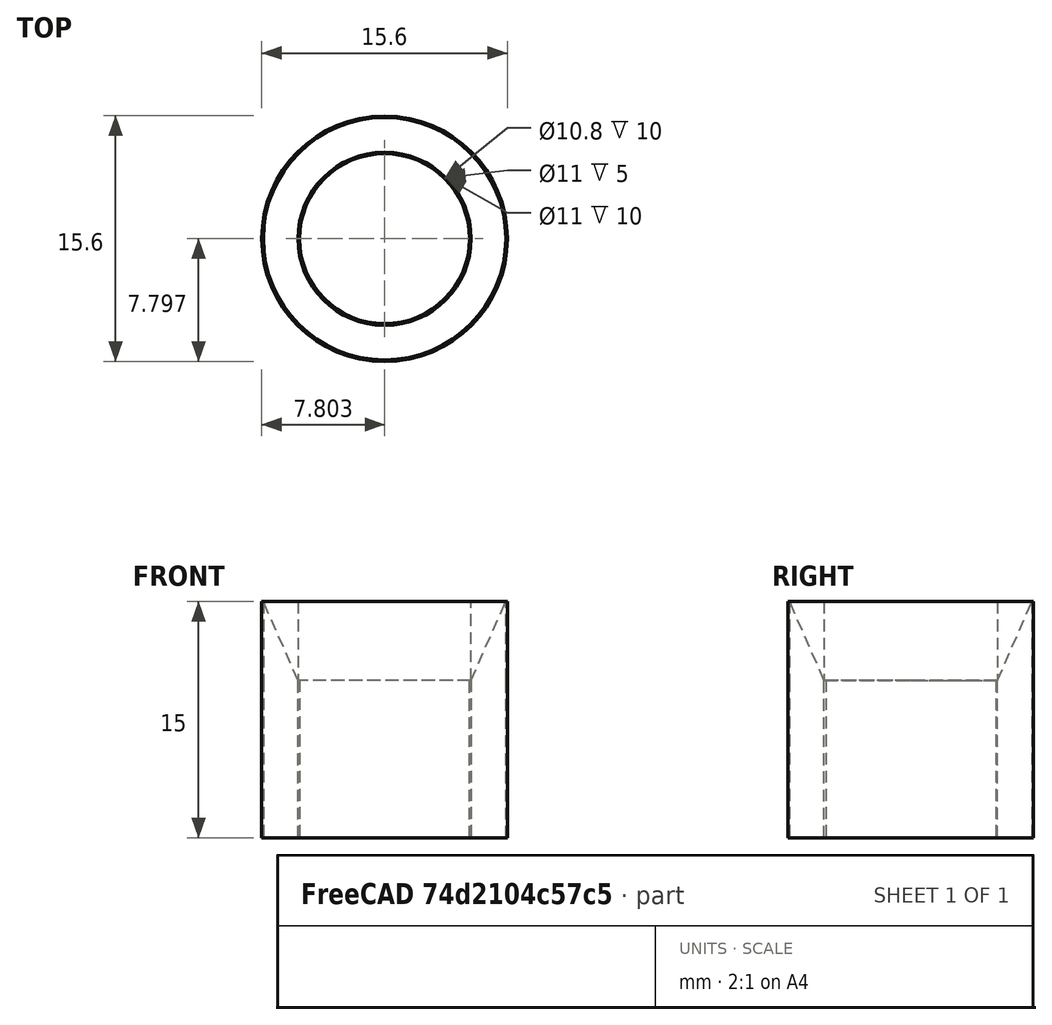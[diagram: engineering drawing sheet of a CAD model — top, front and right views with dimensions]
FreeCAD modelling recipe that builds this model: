
FCSTD DOCUMENT  (FreeCAD 0.18.4R)
Label: spillway.reducer
License: All rights reserved
LicenseURL: http://en.wikipedia.org/wiki/All_rights_reserved
objects: Part::Extrusion×6, Part::Part2DObjectPython×4, Part::Feature×4, Part::Cut×3, Part::MultiFuse×3
note: 20 computed .brp shape members not serialized (recipe doc carries the construction recipe); baked Part::Feature solids carry a one-line shape summary decoded from their .brp

FEATURE [Part::Part2DObjectPython] Circle  # Draft 2D object (typed FeaturePython)
  FirstAngle = 0
  LastAngle = 0
  MakeFace = true
  Placement = pos=(-1.42729,0.617252,0) rot=(0,0,1;0rad)
  Radius = 7.7
FEATURE [Part::Extrusion] Extrusion
  Base = -> Circle
  Dir = (0,0,10)
  DirMode = 0
  FaceMakerClass = Part::FaceMakerBullseye
  LengthFwd = 0
  LengthRev = 0
  Solid = true
  Symmetric = false
FEATURE [Part::Part2DObjectPython] Circle001  # Draft 2D object (typed FeaturePython)
  FirstAngle = 0
  LastAngle = 0
  MakeFace = true
  Placement = pos=(-1.42729,0.617252,10) rot=(0,0,1;0rad)
  Radius = 5.5
  Support = -> [Extrusion]
FEATURE [Part::Extrusion] Extrusion001
  Base = -> Circle001
  Dir = (0,0,-42.4565)
  DirMode = 0
  FaceMakerClass = Part::FaceMakerBullseye
  LengthFwd = 0
  LengthRev = 0
  Solid = true
  Symmetric = false
FEATURE [Part::Cut] Cut
  Base = -> Extrusion
  Tool = -> Extrusion001
FEATURE [Part::Feature] Face
  shape: bbox 15.4 x 15.4 x 2e-07 mm, 1 faces, 0 solids (baked)
FEATURE [Part::Extrusion] Extrusion002
  Base = -> Face
  Dir = (0,0,5)
  DirMode = 0
  FaceMakerClass = Part::FaceMakerBullseye
  LengthFwd = 0
  LengthRev = 0
  Solid = true
  Symmetric = false
FEATURE [Part::MultiFuse] Fusion
  Shapes = -> [Cut,Extrusion002]
FEATURE [Part::Feature] Fusion001
  shape: bbox 15.4 x 15.4 x 15 mm, 4 faces (baked)
FEATURE [Part::Feature] Cone001
  Placement = pos=(-1.42729,0.617252,10) rot=(0,0,1;0rad)
  shape: bbox 15.4 x 15.4 x 5 mm, 3 faces (baked)
FEATURE [Part::Cut] Cut001
  Base = -> Fusion001
  Tool = -> Cone001
FEATURE [Part::Part2DObjectPython] Circle002  # Draft 2D object (typed FeaturePython)
  FirstAngle = 0
  LastAngle = 0
  MakeFace = true
  Placement = pos=(-1.42729,0.617252,0) rot=(1,0,0;3.14159rad)
  Radius = 7.8
  Support = -> [Cut001]
FEATURE [Part::Extrusion] Extrusion003
  Base = -> Circle002
  Dir = (0,0,10)
  DirMode = 0
  FaceMakerClass = Part::FaceMakerBullseye
  LengthFwd = 0
  LengthRev = 0
  Solid = true
  Symmetric = false
FEATURE [Part::MultiFuse] Fusion002
  Shapes = -> [Cut001,Extrusion003]
FEATURE [Part::Part2DObjectPython] Circle003  # Draft 2D object (typed FeaturePython)
  FirstAngle = 0
  LastAngle = 0
  MakeFace = true
  Placement = pos=(-1.42729,0.617252,0) rot=(1,0,0;3.14159rad)
  Radius = 5.4
  Support = -> [Fusion002]
FEATURE [Part::Extrusion] Extrusion004
  Base = -> Circle003
  Dir = (0,0,50.9449)
  DirMode = 0
  FaceMakerClass = Part::FaceMakerBullseye
  LengthFwd = 0
  LengthRev = 0
  Solid = true
  Symmetric = false
FEATURE [Part::Cut] Cut002
  Base = -> Fusion002
  Tool = -> Extrusion004
FEATURE [Part::Feature] Face001
  shape: bbox 15.6 x 15.6 x 2e-07 mm, 1 faces, 0 solids (baked)
FEATURE [Part::Extrusion] Extrusion005
  Base = -> Face001
  Dir = (0,0,5)
  DirMode = 0
  FaceMakerClass = Part::FaceMakerBullseye
  LengthFwd = 0
  LengthRev = 0
  Solid = true
  Symmetric = false
FEATURE [Part::MultiFuse] Fusion003
  Shapes = -> [Cut002,Extrusion005]
